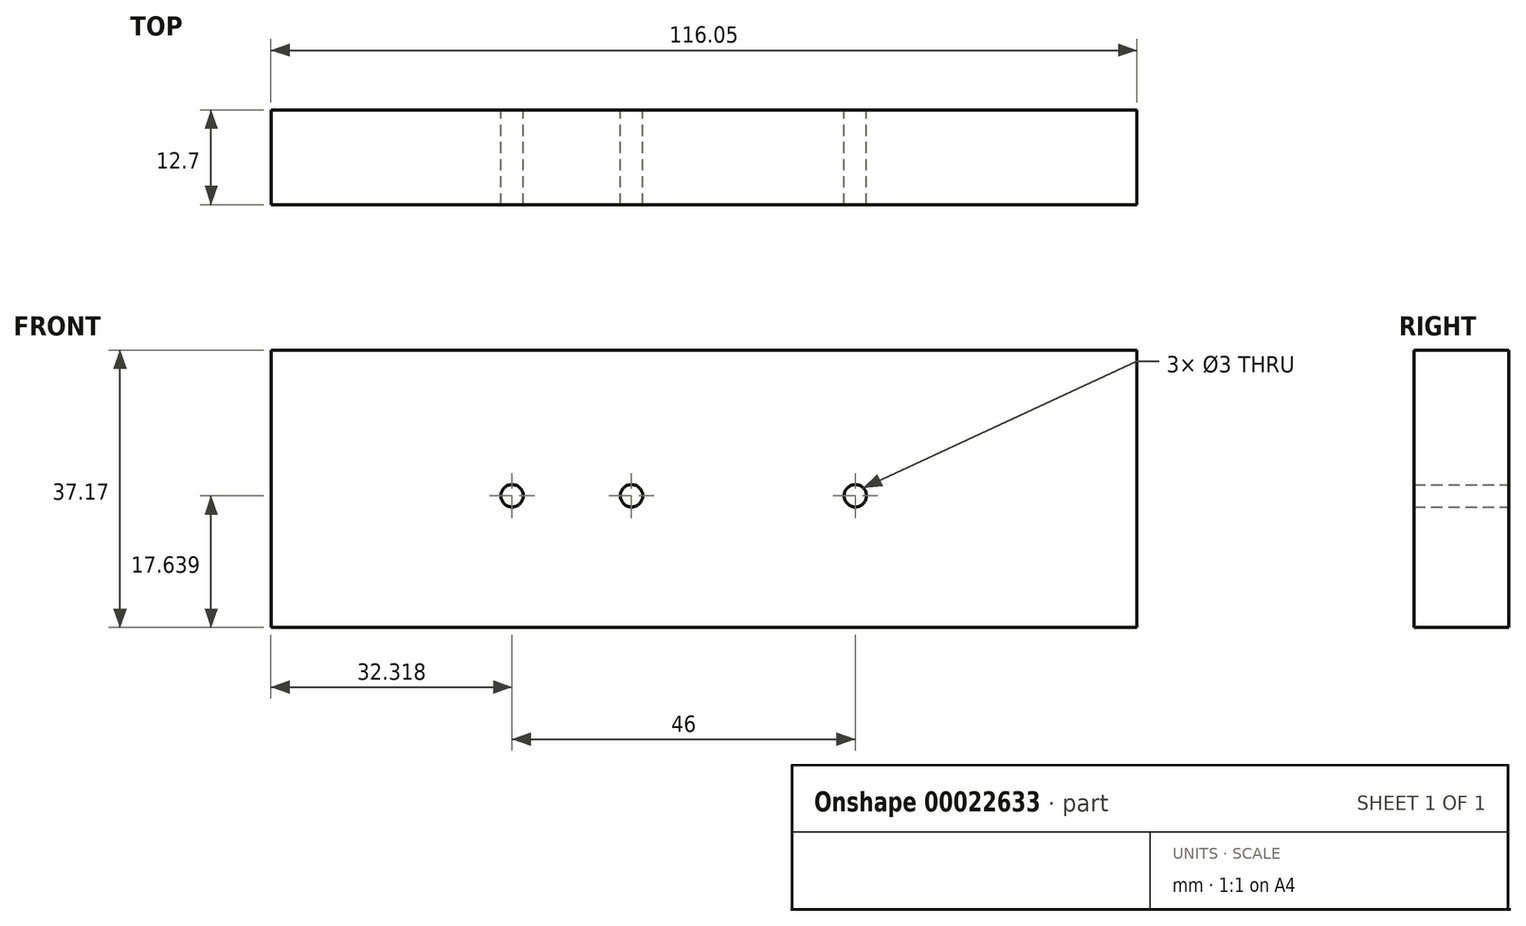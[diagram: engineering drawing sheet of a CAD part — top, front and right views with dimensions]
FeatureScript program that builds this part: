
annotation { "Feature Type Name" : "Feature", "Feature Type Description" : "" }
export const myFeature = defineFeature(function(context is Context, id is Id, definition is map)
    precondition{}
    {
        {
            var Q0;
            Q0=qCreatedBy(makeId("Front.planeOp"),FACE);
            var sketch = newSketch(context, id + "F0", { "sketchPlane" : qUnion([Q0])});
            skCircle(sketch, "E0", {"center": v(-86.64, 17.64) * mm, "radius": 1.5 * mm});
            skCircle(sketch, "E1", {"center": v(-70.64, 17.64) * mm, "radius": 1.5 * mm});
            skCircle(sketch, "E2", {"center": v(-40.64, 17.64) * mm, "radius": 1.5 * mm});
            skPoint(sketch, "E3.end.orphan", {"position": v(-40.64, 0) * mm});
            skPoint(sketch, "E4.end.orphan", {"position": v(-70.64, 0) * mm});
            skPoint(sketch, "E4.start.orphan", {"position": v(-86.64, 0) * mm});
            skLineSegment(sketch, "E5.bottom", {"start": v(-118.96, 0) * mm, "end": v(-2.91, 0) * mm});
            skLineSegment(sketch, "E5.top", {"start": v(-118.96, 37.17) * mm, "end": v(-2.91, 37.17) * mm});
            skLineSegment(sketch, "E5.left", {"start": v(-118.96, 0) * mm, "end": v(-118.96, 37.17) * mm});
            skLineSegment(sketch, "E5.right", {"start": v(-2.91, 0) * mm, "end": v(-2.91, 37.17) * mm});
            skSolve(sketch);
        }
        {
            var Q0;
            Q0=makeQuery(id+"F0.imprint","IMPRINT",FACE,{"disambiguationData":[TD([[makeQuery(id+"F0.imprint","IMPRINT",EDGE,{"derivedFrom":sQuery(id+"F0.wireOp",EDGE,"E0")}),-1.0]])]});
            extrude(context, id + "F1", {"entities" : qUnion([Q0]), "depth" : 12.7 * mm});
        }
    });
